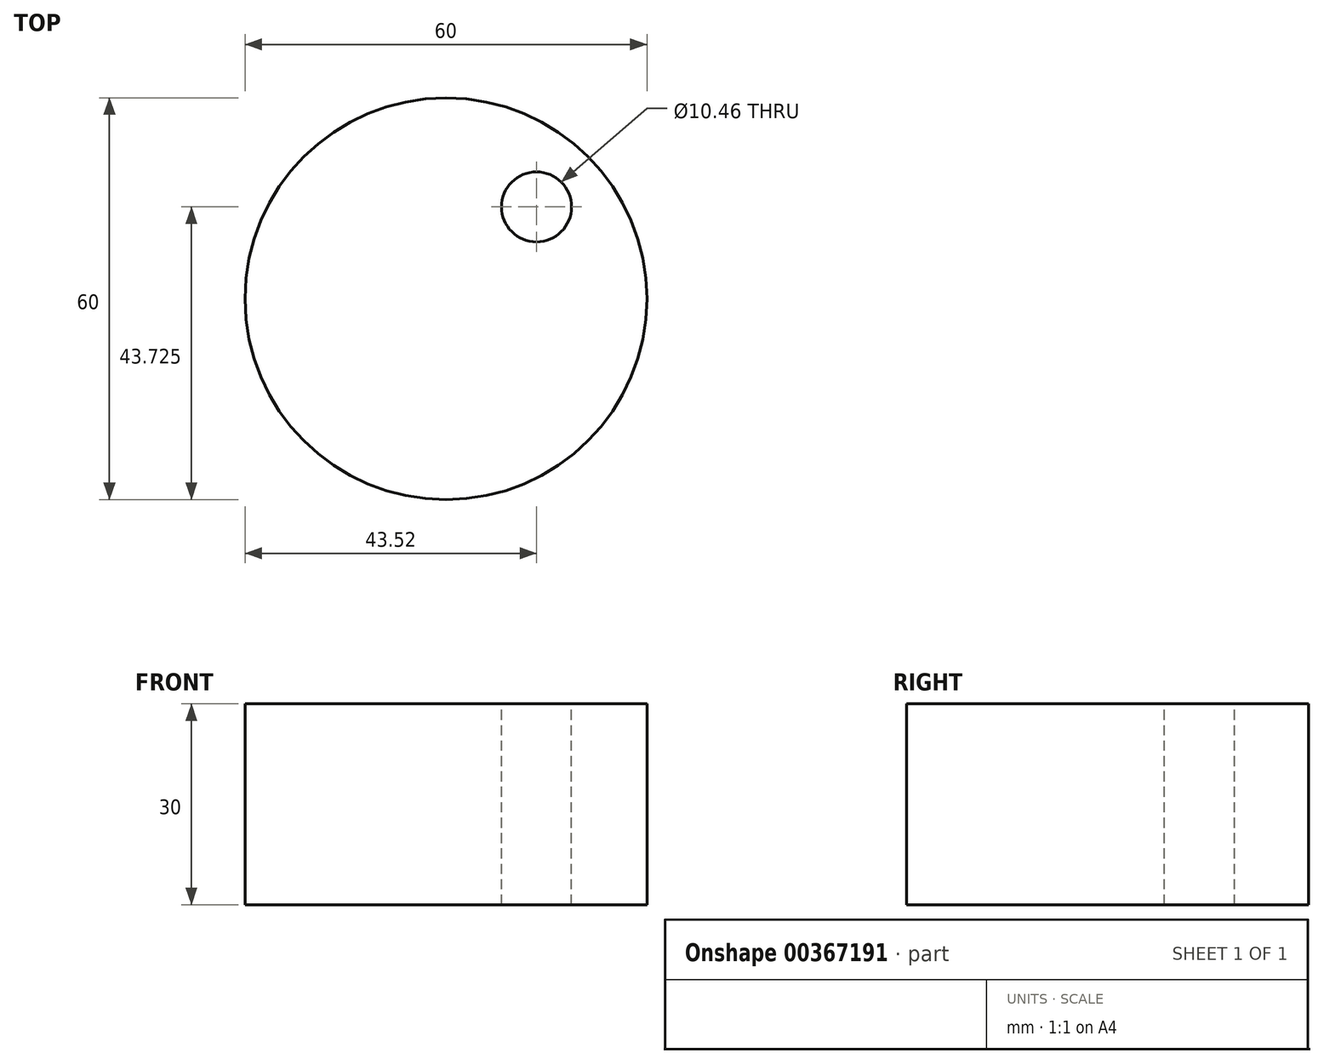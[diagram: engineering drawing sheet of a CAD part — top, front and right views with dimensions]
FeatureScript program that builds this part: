
annotation { "Feature Type Name" : "Feature", "Feature Type Description" : "" }
export const myFeature = defineFeature(function(context is Context, id is Id, definition is map)
    precondition{}
    {
        {
            var Q0;
            Q0=qCreatedBy(makeId("Front.planeOp"),FACE);
            var sketch = newSketch(context, id + "F0", { "sketchPlane" : qUnion([Q0])});
            skLineSegment(sketch, "E0.bottom", {"start": v(0, 0) * mm, "end": v(30, 0) * mm});
            skLineSegment(sketch, "E0.top", {"start": v(0, 30) * mm, "end": v(30, 30) * mm});
            skLineSegment(sketch, "E0.left", {"start": v(0, 0) * mm, "end": v(0, 30) * mm});
            skLineSegment(sketch, "E0.right", {"start": v(30, 0) * mm, "end": v(30, 30) * mm});
            skSolve(sketch);
        }
        {
            var Q0;
            Q0=makeQuery(id+"F0.imprint","IMPRINT",FACE,{"disambiguationData":[TD([[makeQuery(id+"F0.imprint","IMPRINT",EDGE,{"derivedFrom":sQuery(id+"F0.wireOp",EDGE,"E0.bottom")}),1.0]])]});
            var Q1;
            Q1=sQuery(id+"F0.wireOp",EDGE,"E0.left");
            revolve(context, id + "F1", {"entities" : qUnion([Q0]), "axis" : qUnion([Q1]), "revolveType" : RevolveType.FULL});
        }
        {
            var Q0;
            Q0=makeQuery(id+"F1.opRevolve","SWEPT_FACE",FACE,{"disambiguationData":[OSD([sQuery(id+"F0.wireOp",EDGE,"E0.top")])]});
            var sketch = newSketch(context, id + "F2", { "sketchPlane" : qUnion([Q0])});
            skCircle(sketch, "E1", {"center": v(13.52, 13.72) * mm, "radius": 5.23 * mm});
            skSolve(sketch);
        }
        {
            var Q0;
            Q0 = qSketchRegion(id + "F2", true);
            extrude(context, id + "F3", {"entities" : qUnion([Q0]), "operationType" : NewBodyOperationType.REMOVE, "oppositeDirection" : true, "depth" : 46.48 * mm});
        }
    });
